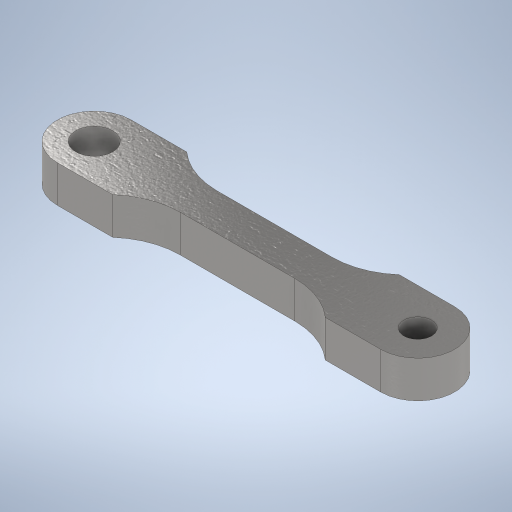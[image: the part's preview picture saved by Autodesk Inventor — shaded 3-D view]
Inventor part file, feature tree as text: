
AUTODESK INVENTOR PART (.ipt)
format: ipt  version: 2024 (Build 280153000, 153)  size: 297,984 bytes
history: native  units: mm
features: sketch x3, hole x2, extrude x1
ambient origin geometry x8: Origin, YZ Plane, XZ Plane, XY Plane, X Axis, Y Axis, Z Axis, Center Point
bodies: Volumenkörper1 (feature_tree)
feature tree (6):
  extrude  "Extrusion1"  Depth=8.0mm
  hole  "Bohrung1"  [1 undecoded]
  hole  "Bohrung2"  [1 undecoded]
  sketch  "Skizze1"  dims[d0=8.0mm d1=8.0mm]
  sketch  "Skizze2"  dims[d2=4.0mm d3=6.0mm]
  sketch  "Skizze3"  dims[d4=6.0mm d5=35.0mm d7=8.0mm d8=4.0mm d9=0.0mm d10=4.0mm d11=6.0mm d12=4.0mm d13=2.0mm d14=90.0deg d15=8.0mm d16=20.594885mm d17=3.0mm d18=6.0mm d19=4.0mm d20=2.0mm d21=90.0deg d22=8.0mm d23=20.594885mm]
note: 2 required parameter values undecoded (feature->parameter linkage not recoverable at this tier; creation-order binding heuristic only, values carry confidence <= 0.55)
